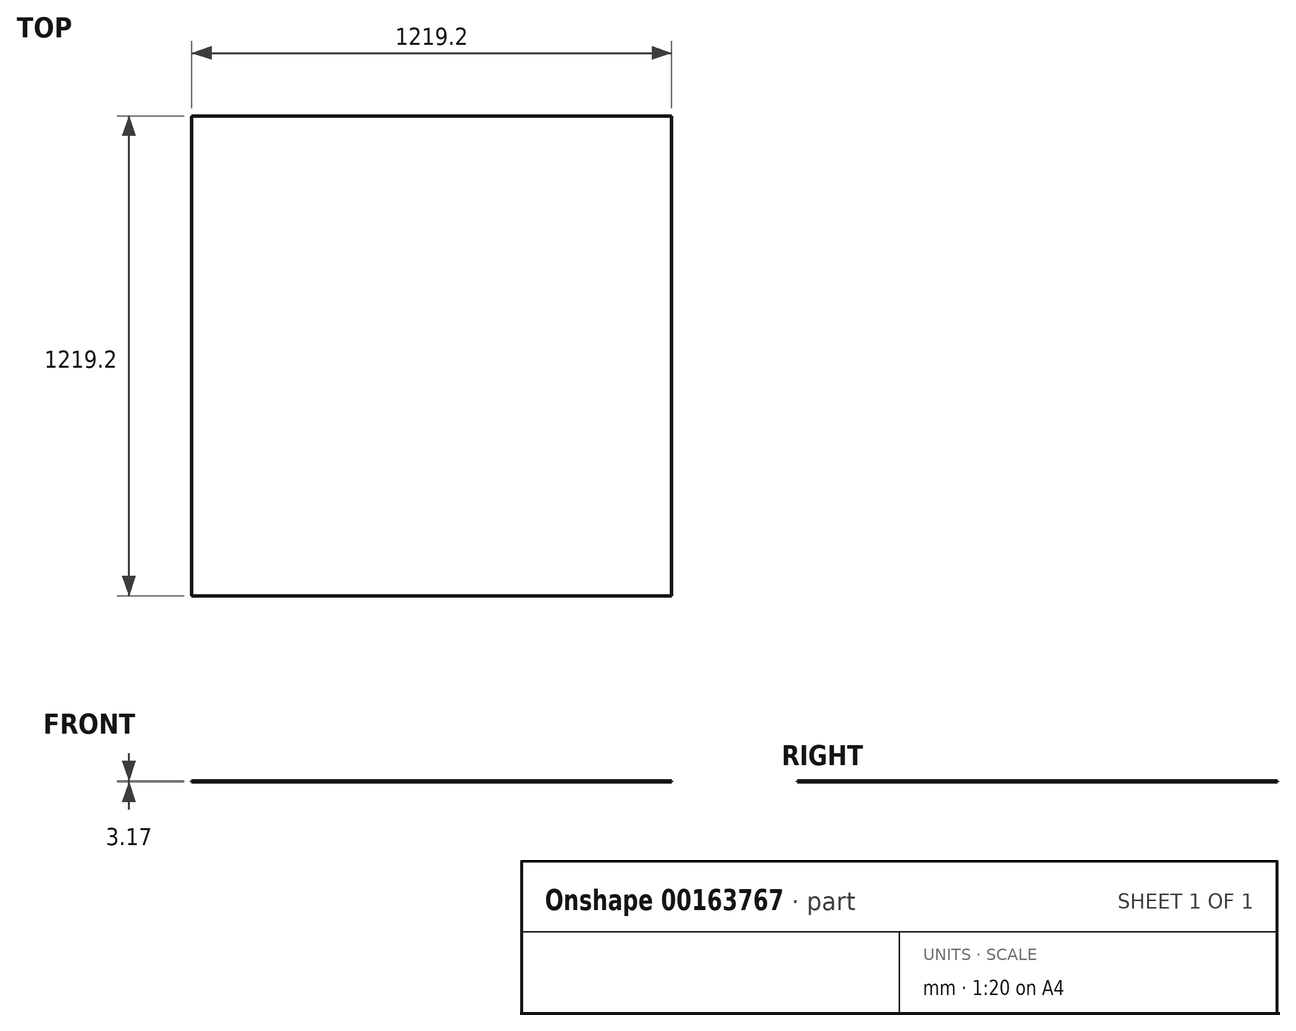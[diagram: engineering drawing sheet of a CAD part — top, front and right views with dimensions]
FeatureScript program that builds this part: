
annotation { "Feature Type Name" : "Feature", "Feature Type Description" : "" }
export const myFeature = defineFeature(function(context is Context, id is Id, definition is map)
    precondition{}
    {
        {
            var Q0;
            Q0=qCreatedBy(makeId("Top.planeOp"),FACE);
            var sketch = newSketch(context, id + "F0", { "sketchPlane" : qUnion([Q0])});
            skLineSegment(sketch, "E0.bottom", {"start": v(609.6, 609.6) * mm, "end": v(-609.6, 609.6) * mm});
            skLineSegment(sketch, "E0.top", {"start": v(609.6, -609.6) * mm, "end": v(-609.6, -609.6) * mm});
            skLineSegment(sketch, "E0.left", {"start": v(609.6, 609.6) * mm, "end": v(609.6, -609.6) * mm});
            skLineSegment(sketch, "E0.right", {"start": v(-609.6, 609.6) * mm, "end": v(-609.6, -609.6) * mm});
            skPoint(sketch, "E0.middle", {"position": v(0, 0) * mm});
            skSolve(sketch);
        }
        {
            var Q0;
            Q0 = qSketchRegion(id + "F0", true);
            extrude(context, id + "F1", {"entities" : qUnion([Q0]), "depth" : 3.17 * mm});
        }
    });
